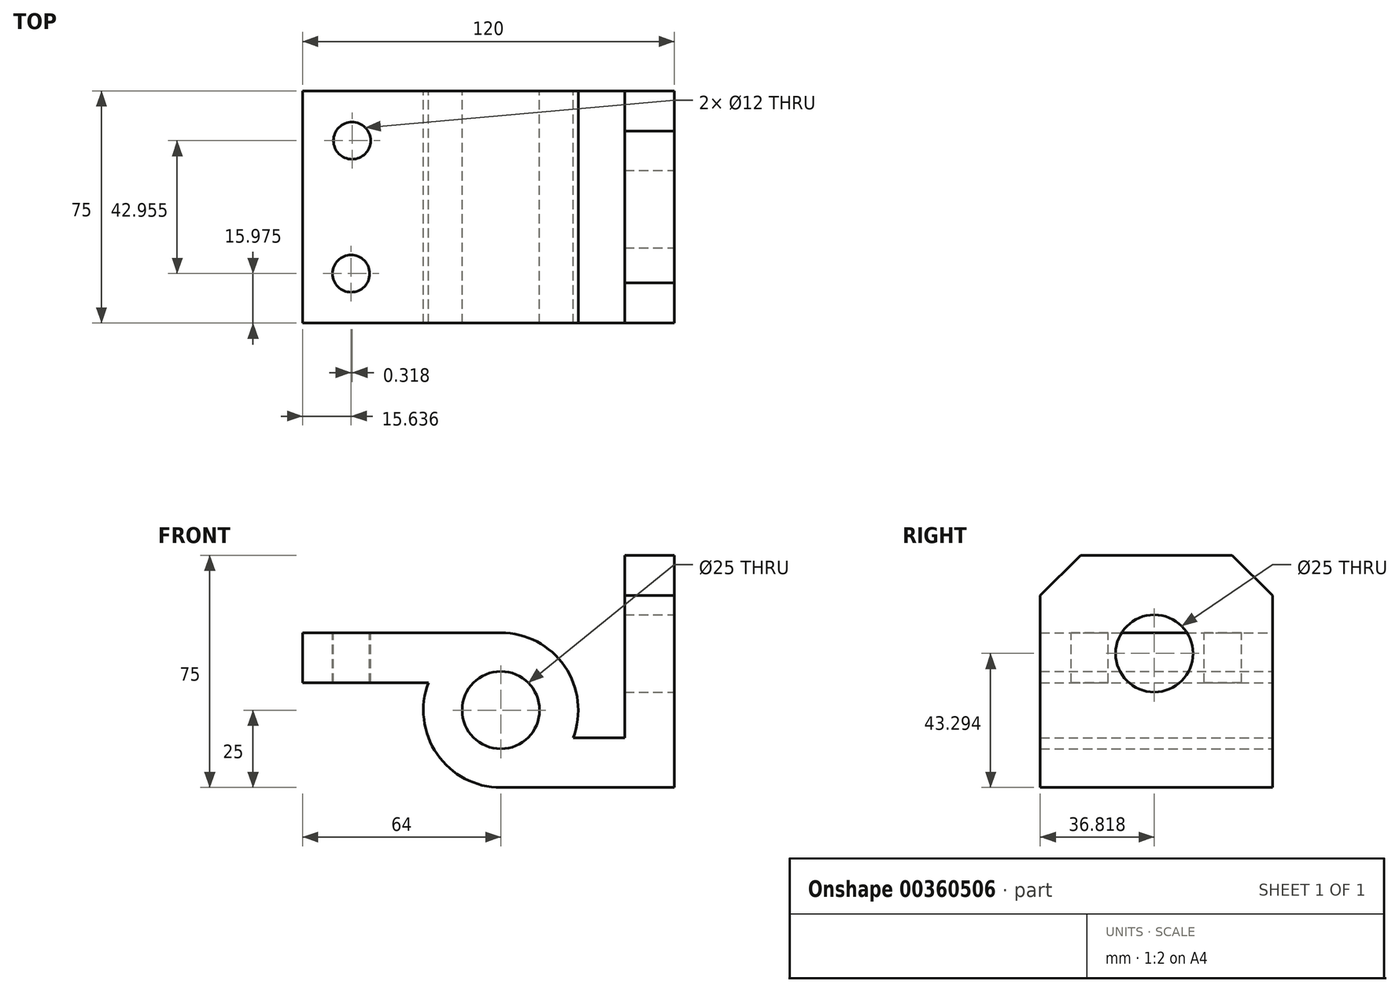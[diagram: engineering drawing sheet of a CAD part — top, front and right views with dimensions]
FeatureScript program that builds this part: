
annotation { "Feature Type Name" : "Feature", "Feature Type Description" : "" }
export const myFeature = defineFeature(function(context is Context, id is Id, definition is map)
    precondition{}
    {
        {
            var Q0;
            Q0=qCreatedBy(makeId("Front.planeOp"),FACE);
            var sketch = newSketch(context, id + "F0", { "sketchPlane" : qUnion([Q0])});
            skLineSegment(sketch, "E0", {"start": v(0, 25) * mm, "end": v(-64, 25) * mm});
            skArc(sketch, "E1", {"start": v(-23.37, 8.89) * mm, "mid": v(-20.58, -14.2) * mm, "end": v(0, -25) * mm});
            skLineSegment(sketch, "E2", {"start": v(-64, 25) * mm, "end": v(-64, 8.89) * mm});
            skLineSegment(sketch, "E3", {"start": v(-64, 8.89) * mm, "end": v(-23.37, 8.89) * mm});
            skLineSegment(sketch, "E4", {"start": v(0, -25) * mm, "end": v(56, -25) * mm});
            skLineSegment(sketch, "E5", {"start": v(56, -25) * mm, "end": v(56, 50) * mm});
            skLineSegment(sketch, "E6", {"start": v(56, 50) * mm, "end": v(40, 50) * mm});
            skLineSegment(sketch, "E7", {"start": v(40, 50) * mm, "end": v(40, -9) * mm});
            skLineSegment(sketch, "E8", {"start": v(40, -9) * mm, "end": v(23.32, -9) * mm});
            skArc(sketch, "E9.trimOffspring", {"start": v(23.32, -9) * mm, "mid": v(20.62, 14.14) * mm, "end": v(0, 25) * mm});
            skCircle(sketch, "E10", {"center": v(0, 0) * mm, "radius": 12.5 * mm});
            skSolve(sketch);
        }
        {
            var Q0;
            Q0 = qSketchRegion(id + "F0", true);
            extrude(context, id + "F1", {"entities" : qUnion([Q0]), "depth" : 75 * mm});
        }
        {
            var Q0;
            Q0=makeQuery(id+"F1.opExtrude","CAP_EDGE",EDGE,{"disambiguationData":[OSD([sQuery(id+"F0.wireOp",EDGE,"E6")])],"isStart":false});
            chamfer(context, id + "F2", {"entities" : qUnion([Q0]), "width" : 13 * mm, "tangentPropagation" : true});
        }
        {
            var Q0;
            Q0=makeQuery(id+"F1.opExtrude","CAP_EDGE",EDGE,{"disambiguationData":[OSD([sQuery(id+"F0.wireOp",EDGE,"E6")])],"isStart":true});
            chamfer(context, id + "F3", {"entities" : qUnion([Q0]), "width" : 13 * mm, "tangentPropagation" : true});
        }
        {
            var Q0;
            Q0=makeQuery(id+"F1.opExtrude","SWEPT_FACE",FACE,{"disambiguationData":[OSD([sQuery(id+"F0.wireOp",EDGE,"E0")])]});
            var sketch = newSketch(context, id + "F4", { "sketchPlane" : qUnion([Q0])});
            skLineSegment(sketch, "E11", {"start": v(-64, 0) * mm, "end": v(-48, 0) * mm, "construction": true});
            skLineSegment(sketch, "E12", {"start": v(-64, -75) * mm, "end": v(-48, -75) * mm, "construction": true});
            skLineSegment(sketch, "E13", {"start": v(-48, 0) * mm, "end": v(-48, -75) * mm, "construction": true});
            skLineSegment(sketch, "E14", {"start": v(-64, -75) * mm, "end": v(-64, -59) * mm, "construction": true});
            skLineSegment(sketch, "E15", {"start": v(-64, -59) * mm, "end": v(0, -59) * mm, "construction": true});
            skLineSegment(sketch, "E16", {"start": v(-64, 0) * mm, "end": v(-64, -16) * mm, "construction": true});
            skLineSegment(sketch, "E17", {"start": v(-64, -16) * mm, "end": v(0, -16) * mm, "construction": true});
            skSolve(sketch);
        }
        {
            var Q0;
            {var subQ0=sQuery(id+"F0.wireOp",EDGE,"E0");Q0=makeQuery(id+"F4.imprint","IMPRINT",FACE,{"disambiguationData":[TD([[makeQuery(id+"F4.imprint","IMPRINT",EDGE,{"derivedFrom":makeQuery(id+"F1.opExtrude","CAP_EDGE",EDGE,{"disambiguationData":[OSD([subQ0])],"isStart":true})}),1.0]])]});}
            var sketch = newSketch(context, id + "F5", { "sketchPlane" : qUnion([Q0])});
            skCircle(sketch, "E18", {"center": v(-48.05, -16.07) * mm, "radius": 6 * mm});
            skCircle(sketch, "E19", {"center": v(-48.36, -59.02) * mm, "radius": 6 * mm});
            skSolve(sketch);
        }
        {
            var Q0;
            Q0 = qSketchRegion(id + "F5", true);
            extrude(context, id + "F6", {"entities" : qUnion([Q0]), "operationType" : NewBodyOperationType.REMOVE, "oppositeDirection" : true, "depth" : 25 * mm});
        }
        {
            var Q0;
            Q0=makeQuery(id+"F1.opExtrude","SWEPT_FACE",FACE,{"disambiguationData":[OSD([sQuery(id+"F0.wireOp",EDGE,"E5")])]});
            var sketch = newSketch(context, id + "F7", { "sketchPlane" : qUnion([Q0])});
            skLineSegment(sketch, "E20", {"start": v(0, 37) * mm, "end": v(-38, 37) * mm, "construction": true});
            skLineSegment(sketch, "E21", {"start": v(-38, 50) * mm, "end": v(-38, 18) * mm, "construction": true});
            skSolve(sketch);
        }
        {
            var Q0;
            {var subQ0=sQuery(id+"F0.wireOp",EDGE,"E5");Q0=makeQuery(id+"F7.imprint","IMPRINT",FACE,{"disambiguationData":[TD([[makeQuery(id+"F7.imprint","IMPRINT",EDGE,{"derivedFrom":makeQuery(id+"F1.opExtrude","CAP_EDGE",EDGE,{"disambiguationData":[OSD([subQ0])],"isStart":false})}),-1.0]])]});}
            var sketch = newSketch(context, id + "F8", { "sketchPlane" : qUnion([Q0])});
            skCircle(sketch, "E22", {"center": v(-38.18, 18.3) * mm, "radius": 12.5 * mm});
            skSolve(sketch);
        }
        {
            var Q0;
            Q0 = qSketchRegion(id + "F8", true);
            extrude(context, id + "F9", {"entities" : qUnion([Q0]), "operationType" : NewBodyOperationType.REMOVE, "oppositeDirection" : true, "depth" : 25 * mm});
        }
    });
